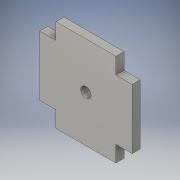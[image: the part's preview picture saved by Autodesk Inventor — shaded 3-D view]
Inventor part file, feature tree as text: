
AUTODESK INVENTOR PART (.ipt)
format: ipt  version: 2016 (Build 200138000, 138)  size: 113,664 bytes
history: native  units: in
note: dims shown in document units (in); Inventor stores cm internally (conversion verified against a paired STEP export)
features: extrude x1, sketch x1
ambient origin geometry x8: Origin, YZ Plane, XZ Plane, XY Plane, X Axis, Y Axis, Z Axis, Center Point
bodies: Body1 (feature_tree)
feature tree (2):
  extrude  "Extrusion2"  Depth=2.2441in
  sketch  "Sketch3"  dims[d15=2.2441in d16=2.2441in d17=1.122in d18=1.122in d19=0.252in d20=0.3937in d21=0.3937in d22=0.3937in d23=0.3937in d24=0.3937in d25=0.3937in d26=0.3937in d27=0.3937in d28=0.1969in d29=0.0in]
